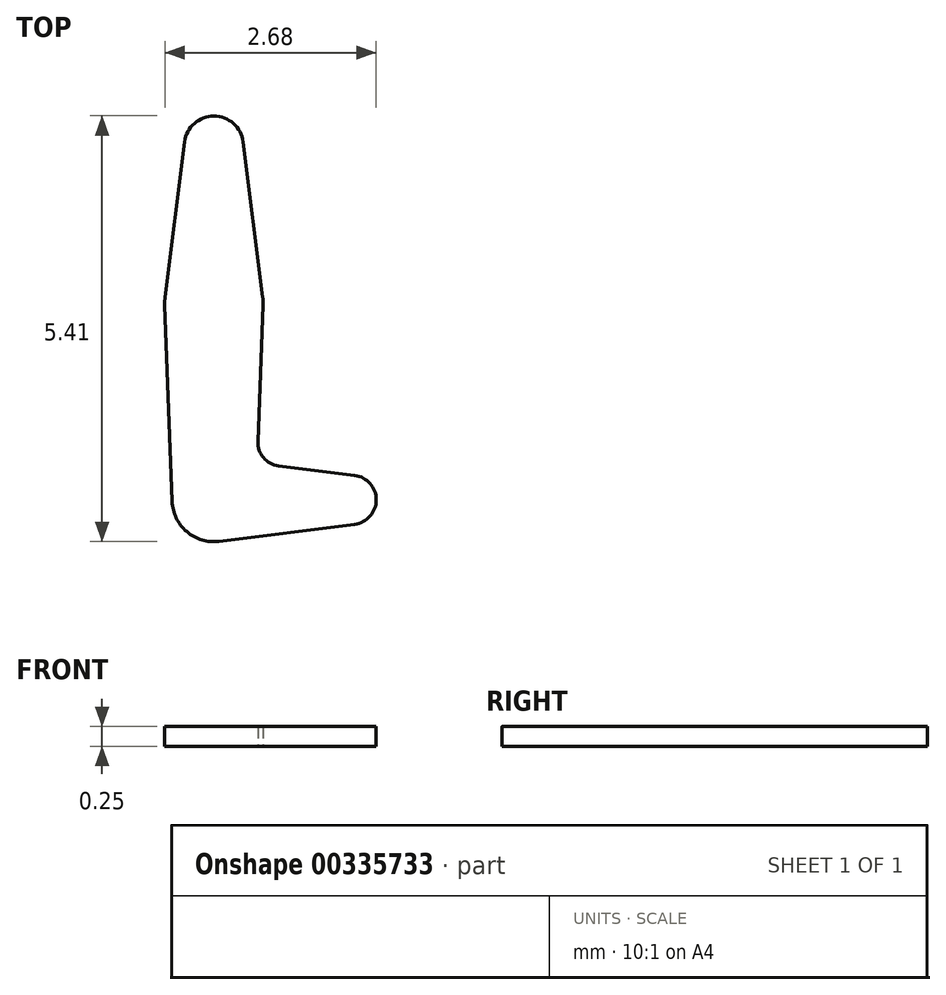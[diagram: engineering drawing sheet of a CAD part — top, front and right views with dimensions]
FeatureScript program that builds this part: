
annotation { "Feature Type Name" : "Feature", "Feature Type Description" : "" }
export const myFeature = defineFeature(function(context is Context, id is Id, definition is map)
    precondition{}
    {
        {
            var Q0;
            Q0=qCreatedBy(makeId("Top.planeOp"),FACE);
            var sketch = newSketch(context, id + "F0", { "sketchPlane" : qUnion([Q0])});
            skLineSegment(sketch, "E0", {"start": v(0, 0) * mm, "end": v(0, 4.5) * mm, "construction": true});
            skCircle(sketch, "E1", {"center": v(0, 0) * mm, "radius": 0.53 * mm});
            skCircle(sketch, "E2", {"center": v(0, 2.5) * mm, "radius": 0.62 * mm});
            skCircle(sketch, "E3", {"center": v(0, 4.5) * mm, "radius": 0.38 * mm});
            skLineSegment(sketch, "E4", {"start": v(0, 0) * mm, "end": v(1.75, 0) * mm, "construction": true});
            skCircle(sketch, "E5", {"center": v(1.75, 0) * mm, "radius": 0.31 * mm});
            skLineSegment(sketch, "E6", {"start": v(-0.37, 4.55) * mm, "end": v(-0.62, 2.58) * mm});
            skLineSegment(sketch, "E7", {"start": v(-0.62, 2.48) * mm, "end": v(-0.53, -0.02) * mm});
            skLineSegment(sketch, "E8", {"start": v(0.37, 4.55) * mm, "end": v(0.62, 2.58) * mm});
            skLineSegment(sketch, "E9", {"start": v(0.62, 2.48) * mm, "end": v(0.56, 0.74) * mm});
            skLineSegment(sketch, "E10", {"start": v(1.79, 0.31) * mm, "end": v(0.82, 0.43) * mm});
            skLineSegment(sketch, "E11", {"start": v(1.79, -0.31) * mm, "end": v(0.07, -0.53) * mm});
            skArc(sketch, "E12.filletArc", {"start": v(0.56, 0.74) * mm, "mid": v(0.63, 0.54) * mm, "end": v(0.82, 0.43) * mm});
            skSolve(sketch);
        }
        {
            var Q0;
            {var subQ0=sQuery(id+"F0.wireOp",EDGE,"E3");var subQ1=makeQuery(id+"F0.imprint","INTERSECT",VERTEX,{"derivedFrom":[subQ0,sQuery(id+"F0.wireOp",EDGE,"E6")]});Q0=makeQuery(id+"F0.imprint","IMPRINT",FACE,{"disambiguationData":[TD([[makeQuery(id+"F0.imprint","IMPRINT",EDGE,{"disambiguationData":[TD([[subQ1,1.0]])],"derivedFrom":subQ0}),1.0]])]});}
            var Q1;
            {var subQ0=sQuery(id+"F0.wireOp",EDGE,"E6");Q1=makeQuery(id+"F0.imprint","IMPRINT",FACE,{"disambiguationData":[TD([[makeQuery(id+"F0.imprint","IMPRINT",EDGE,{"derivedFrom":subQ0}),1.0]])]});}
            var Q2;
            {var subQ0=sQuery(id+"F0.wireOp",EDGE,"E2");var subQ1=makeQuery(id+"F0.imprint","INTERSECT",VERTEX,{"derivedFrom":[subQ0,sQuery(id+"F0.wireOp",EDGE,"E6")]});Q2=makeQuery(id+"F0.imprint","IMPRINT",FACE,{"disambiguationData":[TD([[makeQuery(id+"F0.imprint","IMPRINT",EDGE,{"disambiguationData":[TD([[subQ1,1.0]])],"derivedFrom":subQ0}),1.0]])]});}
            var Q3;
            {var subQ3=sQuery(id+"F0.wireOp",EDGE,"E7");Q3=makeQuery(id+"F0.imprint","IMPRINT",FACE,{"disambiguationData":[TD([[makeQuery(id+"F0.imprint","IMPRINT",EDGE,{"derivedFrom":subQ3}),1.0]])]});}
            var Q4;
            {var subQ0=sQuery(id+"F0.wireOp",EDGE,"E1");var subQ1=makeQuery(id+"F0.imprint","INTERSECT",VERTEX,{"derivedFrom":[subQ0,sQuery(id+"F0.wireOp",EDGE,"E7")]});Q4=makeQuery(id+"F0.imprint","IMPRINT",FACE,{"disambiguationData":[TD([[makeQuery(id+"F0.imprint","IMPRINT",EDGE,{"disambiguationData":[TD([[subQ1,-1.0]])],"derivedFrom":subQ0}),1.0]])]});}
            var Q5;
            {var subQ0=sQuery(id+"F0.wireOp",EDGE,"E5");var subQ1=makeQuery(id+"F0.imprint","INTERSECT",VERTEX,{"derivedFrom":[subQ0,sQuery(id+"F0.wireOp",EDGE,"E10")]});Q5=makeQuery(id+"F0.imprint","IMPRINT",FACE,{"disambiguationData":[TD([[makeQuery(id+"F0.imprint","IMPRINT",EDGE,{"disambiguationData":[TD([[subQ1,-1.0]])],"derivedFrom":subQ0}),1.0]])]});}
            extrude(context, id + "F1", {"entities" : qUnion([Q0, Q1, Q2, Q3, Q4, Q5]), "depth" : 0.25 * mm});
        }
    });
